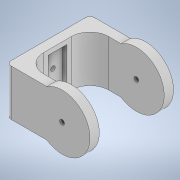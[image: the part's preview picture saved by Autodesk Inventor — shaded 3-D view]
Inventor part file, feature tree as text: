
AUTODESK INVENTOR PART (.ipt)
format: ipt  version: 2022 (Build 260153000, 153)  size: 168,448 bytes
history: native  units: mm
features: sketch x6, extrude x5, fillet x2
ambient origin geometry x8: Origin, YZ Plane, XZ Plane, XY Plane, X Axis, Y Axis, Z Axis, Center Point
bodies: Solid1 (feature_tree)
feature tree (13):
  extrude  "Extrusion1"  Depth=45.0mm
  fillet  "Fillet1"  Radius=10.0mm
  fillet  "Fillet2"  Radius=10.0mm
  extrude  "Extrusion2"  Depth=10.0mm TaperAngle=0.0deg
  extrude  "Extrusion3"  Depth=5.0mm
  extrude  "Extrusion4"  Depth=5.0mm TaperAngle=0.0deg
  sketch  "Sketch5"  dims[d15=5.0mm d16=161.25mm d17=0.0mm]
  extrude  "Extrusion5"  Depth=5.0mm TaperAngle=0.0deg
  sketch  "Sketch1"  dims[d0=45.0mm d1=45.0mm d2=10.0mm d3=10.0mm]
  sketch  "Sketch2"  dims[d4=10.0mm d5=60.0mm d6=0.0mm]
  sketch  "Sketch3"  dims[d7=20.0mm d8=5.0mm]
  sketch  "Sketch4"  dims[d10=5.0mm d12=161.25mm d13=0.0mm]
  sketch  "Sketch6"  dims[d18=5.0mm d19=161.25mm d20=0.0mm d21=20.0mm d22=10.0mm d23=40.0mm d24=20.0mm d25=40.0mm d26=90.0deg d27=5.0mm d28=0.0mm]
